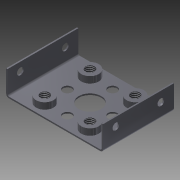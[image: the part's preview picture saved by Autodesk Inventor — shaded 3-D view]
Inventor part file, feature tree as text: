
AUTODESK INVENTOR PART (.ipt)
format: ipt  version: 2012 (Build 160160000, 160)  size: 192,512 bytes
history: native  units: mm
features: sheet_metal_op x7, sketch x7, extrude x4, thread x4, other x3
ambient origin geometry x8: Origin, YZ Plane, XZ Plane, XY Plane, X Axis, Y Axis, Z Axis, Center Point
bodies: Solid1 (feature_tree)
feature tree (25):
  sheet_metal_op  "Face1"
  sheet_metal_op  "Flange1"
  sheet_metal_op  "Flange2"
  extrude  "Extrusion1"  Depth=34.46mm
  extrude  "Extrusion2"  Depth=25.2mm
  extrude  "Extrusion3"  Depth=0.5mm
  thread  "Thread1"  [1 undecoded]
  thread  "Thread2"  [1 undecoded]
  thread  "Thread3"  [1 undecoded]
  thread  "Thread4"  [1 undecoded]
  extrude  "Extrusion4"  Depth=0.5mm
  sketch  "Sketch1"  dims[d0=17.23mm d1=34.46mm]
  other  "Plate1"
  sketch  "Sketch4"  dims[d2=12.6mm d3=25.2mm]
  other  "Plate2"
  sheet_metal_op  "Bend1"
  sheet_metal_op  "Corner1"
  sketch  "Sketch5"  dims[d4=0.5mm d6=0.5mm d7=0.25mm d8=1.0mm d9=0.5mm d10=8.75mm d11=90.0deg d12=0.5mm]
  other  "Plate3"
  sheet_metal_op  "Bend2"
  sheet_metal_op  "Corner2"
  sketch  "Sketch6"  dims[d13=2.0mm d14=0.5mm]
  sketch  "Sketch7"  dims[d15=0.5mm]
  sketch  "Sketch8"  dims[d16=0.5mm]
  sketch  "Sketch9"  dims[d17=0.25mm d18=1.0mm d19=0.5mm d20=8.75mm d21=90.0deg d22=0.5mm d23=2.0mm d24=0.5mm d25=0.5mm d26=3.3mm d27=8.0mm d29=4.56mm d30=4.56mm d31=8.04mm d32=8.04mm d33=8.04mm d34=10.0mm d35=0.0mm d36=3.2mm d37=10.0mm d38=0.0mm d39=6.2mm d40=2.28mm d41=0.0mm d42=10.0mm d43=0.0mm d44=10.0mm d45=0.0mm d46=10.0mm d47=0.0mm d48=10.0mm d49=0.0mm d50=2.4mm d51=16.0mm d52=4.63mm d53=10.0mm d54=0.0mm]
note: 4 required parameter values undecoded (feature->parameter linkage not recoverable at this tier; creation-order binding heuristic only, values carry confidence <= 0.55)
